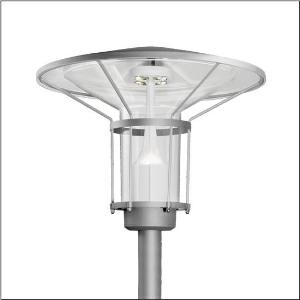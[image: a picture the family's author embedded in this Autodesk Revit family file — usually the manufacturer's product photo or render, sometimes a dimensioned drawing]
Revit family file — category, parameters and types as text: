
# Revit family: laterne_classic_iq___st1_2a_5xa5245mf14hp_5b72
name_source: partatom
category: Lighting Fixtures
units: mm (PartAtom-declared; Revit-internal decimal feet)

## family parameters
Cut with Voids When Loaded = No
Host = Face
Light Source = No
Part Type = Normal
Room Calculation Point = No
Round Connector Dimension = Use Diameter
Shared = No

## types (1)
- --- (1 x LED, 3800 lm, 33.6 W, 2700K)
    Apparent Load = 34 VA
    CIE Flux Codes = 22 60 93 98 100
    Color Rendering = 70
    Color Temperature = 2700K
    Default Elevation = 1800 mm
    Description = Lantern Classic iQ, mast luminaire, Module 540 iQ-SR, primary light control with 3 zone facetted reflector, of plastic, silver coated, highly specular, structured, primary optical cover: cover, of PMMA, transparent, light distribution: ST1.2a, light emission: direct distribution, primary light characteristic: asymmetric, installation type: post-top, LED, High Power LED, rated luminous flux: 3.800lm, luminous efficacy: 113lm/W, light colour: 727, colour temperature: 2700K, control gear: ECG iQ, control: pre-setting: logarithmic dimming characteristic, Street-Remote, Auto-Match, Temp-Guard, Lumen-Switch, Night-Set, Smart-Wire, Light-Fading, Desk-Remote (wireless, voltage-free reading and setting of iQ features in the workshop via application-optimized NFC function/RFID function), optimised constant luminous flux control (CLO 2.0), with terminal, 6-pole, max. 2.5mm², mains connection: 230..240V, AC, 50/60Hz, start of lifetime: 34W, end of service life: 36W, reduction: 15W, luminaire housing, upper part, of glass-fibre reinforced polyester, coated, Siteco® metallic grey (DB 702S), diameter: 750mm, height: 596mm, spigot size: d x l = 76 x 70mm (post-top) | with reducer (optional accessory) 60 x 70mm, post-top mast mounting element, of diecast aluminium, coated, Siteco® metallic grey (DB 702S), Module 540 iQ-SR, traffic white (RAL 9016), equipment: Power, protection rating (complete): IP65, insulation class (complete): insulation class II (safety insulation), certification: CE, ENEC, VDE, packaging unit: 1 piece

Light Distribution: ST1.2a
    Height = 596 mm
    Lamp = 1 x LED
    Lamp Light Flux = 3800 lm
    Lamp Power = 33.6 W
    Lamp count = 1
    Length = 750 mm
    Luminous efficacy = 113 lm/W
    Manufacturer = Siteco
    ModVariant = No
    Model = 5XA5245MF14HP
    Number of Poles = 1
    OnlyDefault = Yes
    Power Factor = 1
    Product Name = Laterne Classic iQ | ST1.2a
    Product group = mast luminaire | pylon top
    ProductGroupID = 6100
    Protection Class = Protection class II
    Protection Degree = IP 65
    RLX_Detail_Level = 1
    RLX_Emergency_Light_Flux = 0 lm
    RLX_Emergency_Type = 0
    RLX_Emergency_Type_DB = No
    RlxData = <blob elided: 65173 chars, md5=e2db172b>
    Socket = socket
    Standby Power = 0 W
    System Light Flux = 3800 lm
    System Power = 34 W
    Type Comments = factory setting: luminous flux: 100 % | dim-lin: 254 | 695 mA
    Type Image = l_1006052.jpg
    URL = http://relux.com
    VarID = @adj_123027
    Voltage = 0 V
    Weight = 0.00 kg
    Width = 0 mm  [stored 0 ft]

note: [stored X ft] marks values corroborated as IEEE doubles in the binary element streams (Revit-internal decimal feet)

## geometry (parser evidence)
native form markers: Blend x4, Sweep x9
no freeform markers — native parametric forms only
